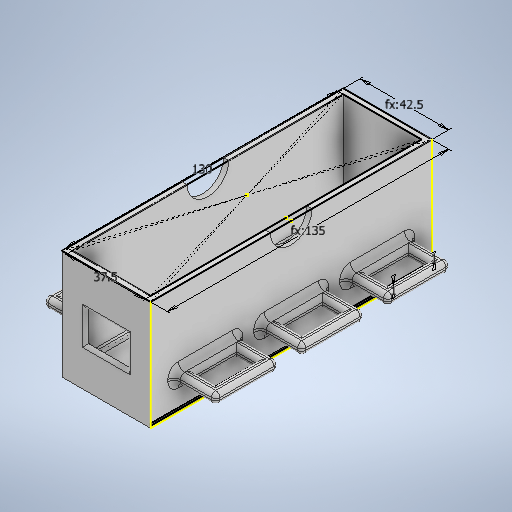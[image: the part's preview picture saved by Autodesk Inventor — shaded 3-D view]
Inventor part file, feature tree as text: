
AUTODESK INVENTOR PART (.ipt)
format: ipt  version: 2025 (Build 290162010, 162A)  size: 699,392 bytes
history: native  units: in
note: dims shown in document units (in); Inventor stores cm internally (conversion verified against a paired STEP export)
features: sketch x11, extrude x9, mirror x9, fillet x7, move_body x6, direct_edit x5
ambient origin geometry x8: Origin, YZ Plane, XZ Plane, XY Plane, X Axis, Y Axis, Z Axis, Center Point
bodies: Solid1 (feature_tree)
feature tree (47):
  sketch  "Sketch1"  dims[d0=1.4764in d1=5.1181in]
  extrude  "Extrusion1"  Depth=5.1181in
  extrude  "Extrusion2"  Depth=5.315in
  extrude  "Extrusion3"  Depth=1.9685in TaperAngle=0.0deg
  extrude  "Extrusion4"  Depth=0.1969in
  sketch  "Sketch4"  dims[d8=1.1811in d9=0.1969in]
  sketch  "Sketch5"  dims[d10=0.5167in d11=2.0669in d12=1.1811in d13=0.1969in d14=1.1811in d15=0.1969in]
  sketch  "Sketch6"  dims[d16=0.4429in d17=0.4429in]
  extrude  "Extrusion5"  Depth=2.0669in
  direct_edit  "Direct Edit1"
  fillet  "Fillet1"  Radius=1.1811in
  fillet  "Fillet2"  Radius=1.1811in
  fillet  "Face Fillet1"
  fillet  "Face Fillet2"
  fillet  "Face Fillet3"
  mirror  "Mirror4"
  mirror  "Mirror5"
  mirror  "Mirror6"
  mirror  "Mirror7"
  mirror  "Mirror8"
  sketch  "Sketch9"  dims[d25=0.3937in d26=0.7874in]
  extrude  "Extrusion7"  Depth=0.4429in
  extrude  "Extrusion8"  Depth=0.7874in TaperAngle=0.0deg
  fillet  "Fillet3"  Radius=0.7874in
  fillet  "Fillet4"  Radius=1.1811in
  extrude  "Extrusion9"  Depth=0.1969in
  mirror  "Mirror9"
  direct_edit  "Direct Edit3"
  direct_edit  "Direct Edit4"
  direct_edit  "Direct Edit5"
  direct_edit  "Direct Edit2"
  mirror  "Mirror1"
  extrude  "Extrusion6"  Depth=0.7874in
  mirror  "Mirror2"
  mirror  "Mirror3"
  sketch  "Sketch2"  dims[d2=1.6732in d3=5.315in]
  sketch  "Sketch3"  dims[d4=2.0669in d5=0.0in d6=1.9685in d7=0.0in]
  sketch  "Sketch7"  dims[d18=0.4429in d19=0.7874in d20=0.0in d21=0.7874in d22=1.1811in]
  sketch  "Sketch8"  dims[d23=0.1969in d24=0.1969in]
  sketch  "Sketch10"  dims[d27=1.624in]
  sketch  "Sketch11"  dims[d28=0.3937in d29=0.7874in d30=0.3937in d31=0.7874in d32=0.7874in d33=0.0in d34=0.0394in d35=0.0394in d36=0.0394in d37=0.1181in d38=0.0394in d39=0.0in d40=0.0in d41=0.0in d42=0.0197in d43=0.0197in d44=0.0394in d45=0.0394in d46=0.3937in d47=0.0394in d48=0.0in d49=0.0787in d50=0.1181in d51=0.1181in d52=0.1181in d53=0.0787in d54=0.0in d55=0.0in d56=0.5906in d57=0.7087in d58=1.6732in d59=0.5413in d60=0.0984in d61=0.7874in d62=0.5906in d63=2.0669in d64=0.7382in d65=0.4429in d66=0.3937in d67=0.0in d68=0.3937in d69=0.0in d70=0.0591in d71=0.0591in d72=0.7874in d73=0.3937in d74=0.3937in d75=0.0in d76=2.2638in d77=5.315in d78=0.3937in d79=0.0in d80=-0.0197in d81=0.0in d82=0.0in d83=0.0197in d84=0.0in d85=0.0in d86=0.0098in d87=0.0in d88=0.0in d89=0.0098in d90=0.0in d91=0.0in]
  move_body  "Move1"
  move_body  "Move2"
  move_body  "Move3"
  move_body  "Move4"
  move_body  "Move5"
  move_body  "Move6"
